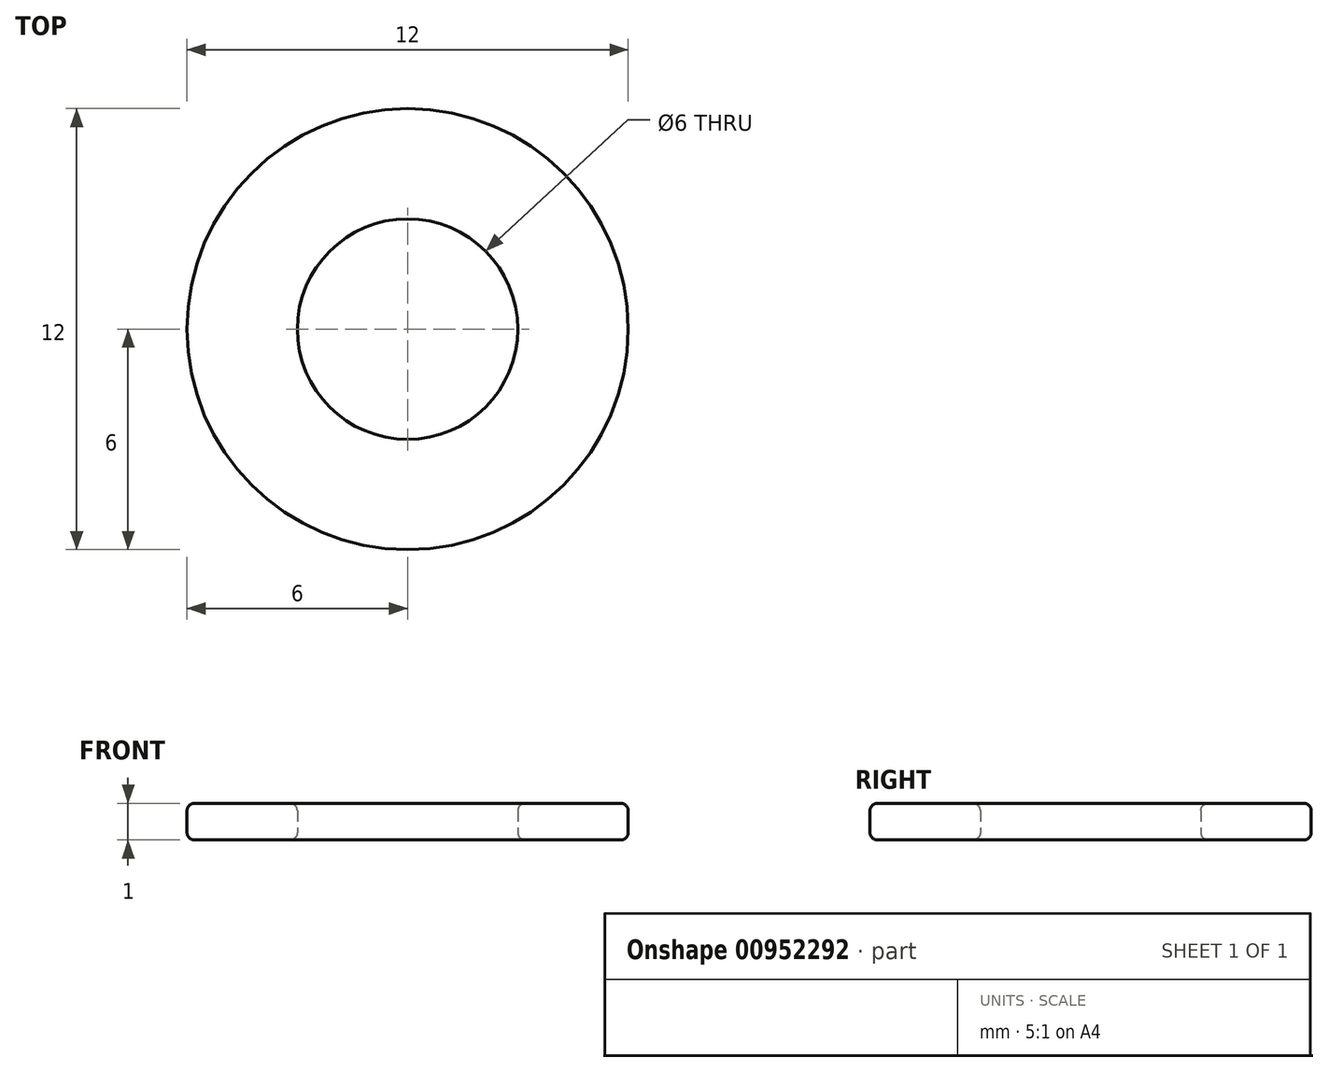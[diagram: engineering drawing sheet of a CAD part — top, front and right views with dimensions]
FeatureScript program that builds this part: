
annotation { "Feature Type Name" : "Feature", "Feature Type Description" : "" }
export const myFeature = defineFeature(function(context is Context, id is Id, definition is map)
    precondition{}
    {
        {
            var Q0;
            Q0=qCreatedBy(makeId("Top.planeOp"),FACE);
            cPlane(context, id + "F0", {"entities" : qUnion([Q0]), "cplaneType" : CPlaneType.OFFSET, "offset" : 0 * mm, "width" : 150 * mm, "height" : 150 * mm});
        }
        {
            var Q0;
            Q0=qCreatedBy(id+"F0.planeOp",FACE);
            var sketch = newSketch(context, id + "F1", { "sketchPlane" : qUnion([Q0])});
            skCircle(sketch, "E0", {"center": v(0, 0) * mm, "radius": 6 * mm});
            skCircle(sketch, "E1", {"center": v(0, 0) * mm, "radius": 3 * mm});
            skSolve(sketch);
        }
        {
            var Q0;
            Q0=qSketchRegion(id+"F1",true);
            extrude(context, id + "F2", {"entities" : qUnion([Q0]), "depth" : 1 * mm, "offsetDistance" : 25 * mm});
        }
        {
            var Q0;
            Q0=makeQuery(id+"F2.opExtrude","SWEPT_FACE",FACE,{"disambiguationData":[OSD([sQuery(id+"F1.wireOp",EDGE,"E0")])]});
            var Q1;
            Q1=makeQuery(id+"F2.opExtrude","CAP_FACE",FACE,{"disambiguationData":[OSD([sQuery(id+"F1.wireOp",EDGE,"E0"),sQuery(id+"F1.wireOp",EDGE,"E1")])],"isStart":true});
            var Q2;
            Q2=makeQuery(id+"F2.opExtrude","CAP_FACE",FACE,{"disambiguationData":[OSD([sQuery(id+"F1.wireOp",EDGE,"E0"),sQuery(id+"F1.wireOp",EDGE,"E1")])],"isStart":false});
            fillet(context, id + "F3", {"entities" : qUnion([Q0, Q1, Q2]), "tangentPropagation" : true, "radius" : 0.2 * mm, "defaultsChanged" : false, "vertexSettings" : [], "allowEdgeOverflow" : false});
        }
    });
